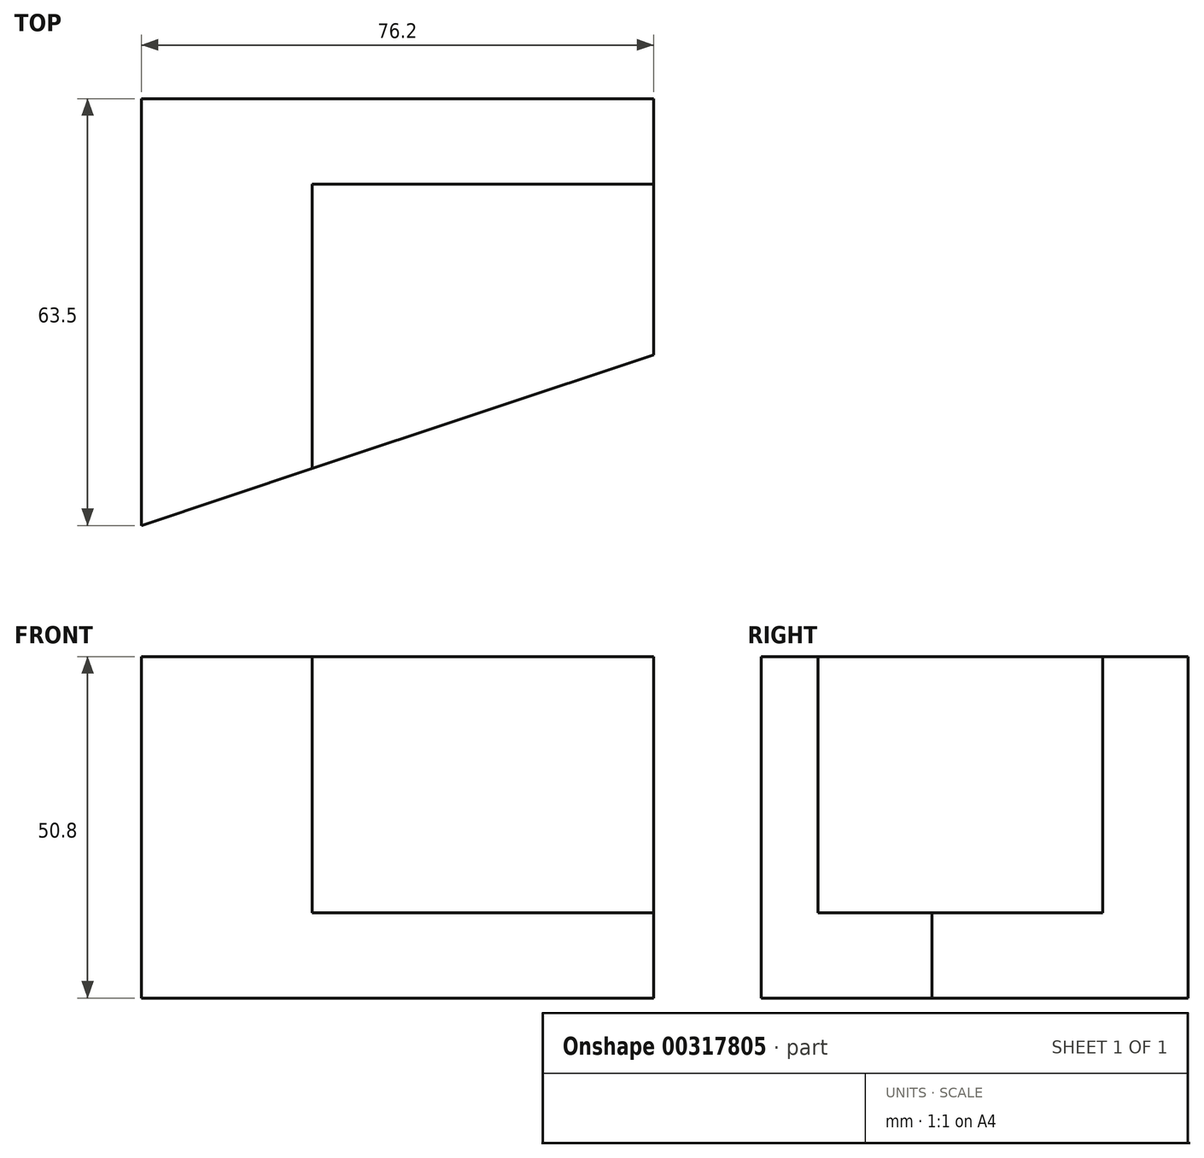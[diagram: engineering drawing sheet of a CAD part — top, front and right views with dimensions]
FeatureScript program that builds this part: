
annotation { "Feature Type Name" : "Feature", "Feature Type Description" : "" }
export const myFeature = defineFeature(function(context is Context, id is Id, definition is map)
    precondition{}
    {
        {
            var Q0;
            Q0=qCreatedBy(makeId("Front.planeOp"),FACE);
            var sketch = newSketch(context, id + "F0", { "sketchPlane" : qUnion([Q0])});
            skLineSegment(sketch, "E0", {"start": v(0, 0) * mm, "end": v(0, 50.8) * mm});
            skLineSegment(sketch, "E1", {"start": v(0, 50.8) * mm, "end": v(76.2, 50.8) * mm});
            skLineSegment(sketch, "E2", {"start": v(76.2, 50.8) * mm, "end": v(76.2, 0) * mm});
            skLineSegment(sketch, "E3", {"start": v(76.2, 0) * mm, "end": v(0, 0) * mm});
            skLineSegment(sketch, "E4", {"start": v(25.4, 50.8) * mm, "end": v(25.4, 12.7) * mm});
            skLineSegment(sketch, "E5", {"start": v(25.4, 12.7) * mm, "end": v(76.2, 12.7) * mm});
            skSolve(sketch);
        }
        {
            var Q0;
            Q0 = qSketchRegion(id + "F0", true);
            extrude(context, id + "F1", {"entities" : qUnion([Q0]), "depth" : 63.5 * mm});
        }
        {
            var Q0;
            Q0=makeQuery(id+"F1.opExtrude","SWEPT_FACE",FACE,{"disambiguationData":[OSD([sQuery(id+"F0.wireOp",EDGE,"E1")])]});
            var sketch = newSketch(context, id + "F2", { "sketchPlane" : qUnion([Q0])});
            skLineSegment(sketch, "E6", {"start": v(76.2, -12.7) * mm, "end": v(25.4, -12.7) * mm});
            skLineSegment(sketch, "E7", {"start": v(25.4, -12.7) * mm, "end": v(25.4, -55.03) * mm});
            skLineSegment(sketch, "E8", {"start": v(76.2, 0) * mm, "end": v(76.2, -38.1) * mm});
            skLineSegment(sketch, "E9", {"start": v(0, -63.5) * mm, "end": v(76.2, -38.1) * mm});
            skLineSegment(sketch, "E10", {"start": v(76.2, 0) * mm, "end": v(0, 0) * mm});
            skLineSegment(sketch, "E11", {"start": v(0, 0) * mm, "end": v(0, -63.5) * mm});
            skPoint(sketch, "E12.orphan", {"position": v(25.4, -63.5) * mm});
            skSolve(sketch);
        }
        {
            var Q0;
            {var subQ1=sQuery(id+"F0.wireOp",EDGE,"E1");var subQ2=makeQuery(id+"F1.opExtrude","CAP_EDGE",EDGE,{"disambiguationData":[OSD([subQ1])],"isStart":false});Q0=makeQuery(id+"F2.imprint","IMPRINT",FACE,{"disambiguationData":[TD([[makeQuery(id+"F2.imprint","IMPRINT",EDGE,{"derivedFrom":subQ2}),1.0]])]});}
            extrude(context, id + "F3", {"entities" : qUnion([Q0]), "operationType" : NewBodyOperationType.REMOVE, "endBound" : BoundingType.THROUGH_ALL, "oppositeDirection" : true, "depth" : 25.4 * mm});
        }
        {
            var Q0;
            {var subQ0=sQuery(id+"F2.wireOp",EDGE,"E6");Q0=makeQuery(id+"F2.imprint","IMPRINT",FACE,{"disambiguationData":[TD([[makeQuery(id+"F2.imprint","IMPRINT",EDGE,{"derivedFrom":subQ0}),1.0]])]});}
            extrude(context, id + "F4", {"entities" : qUnion([Q0]), "operationType" : NewBodyOperationType.REMOVE, "oppositeDirection" : true, "depth" : 38.1 * mm});
        }
    });
